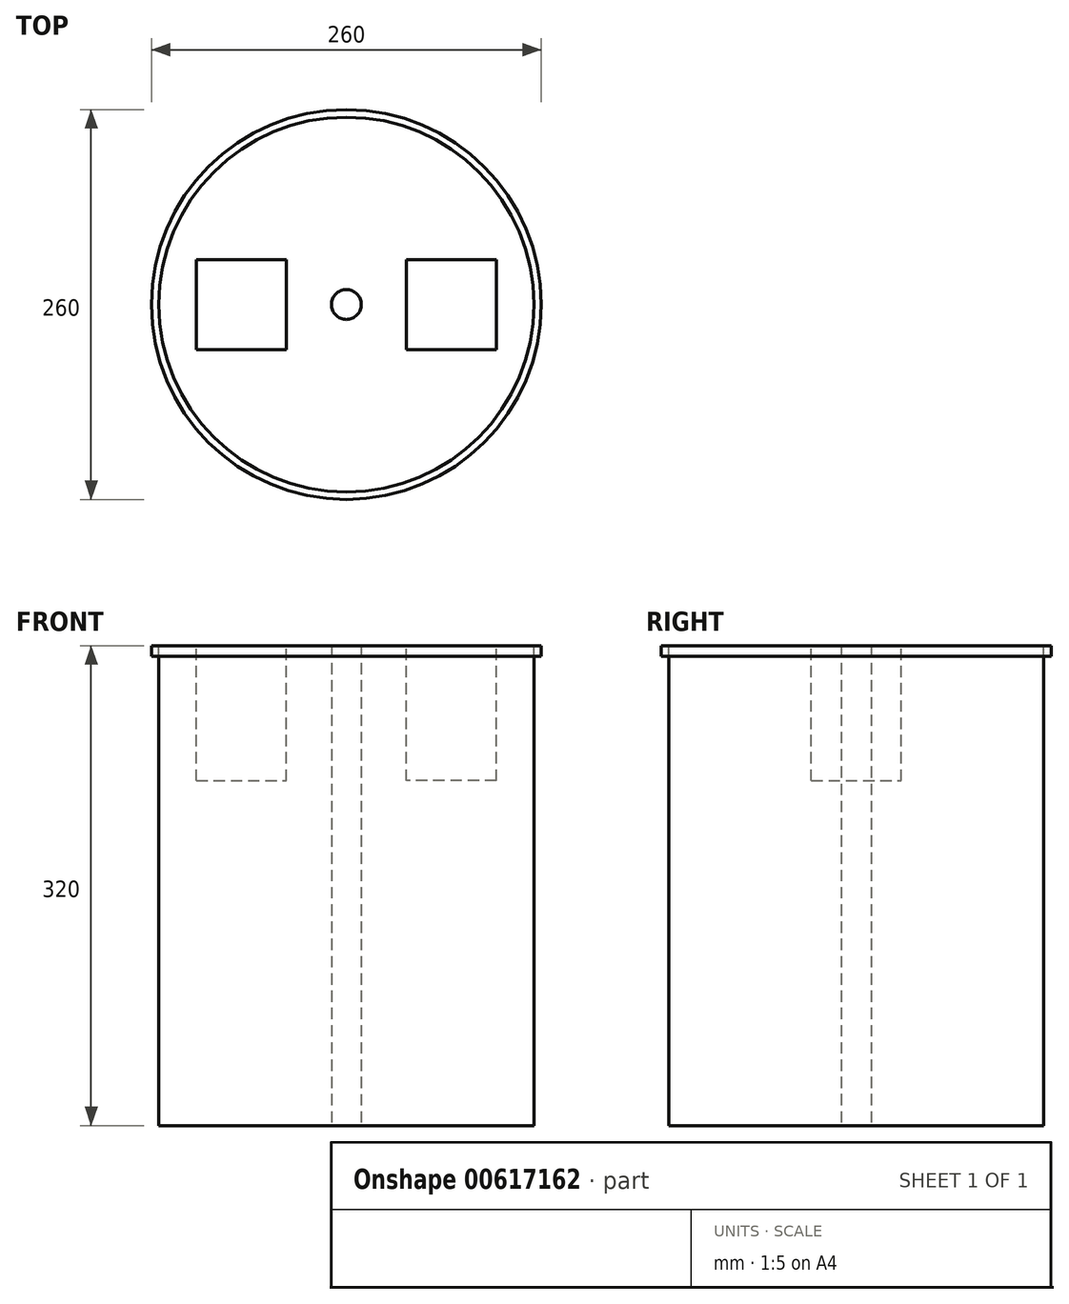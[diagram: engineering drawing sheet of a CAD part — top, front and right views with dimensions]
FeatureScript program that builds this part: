
annotation { "Feature Type Name" : "Feature", "Feature Type Description" : "" }
export const myFeature = defineFeature(function(context is Context, id is Id, definition is map)
    precondition{}
    {
        {
            var Q0;
            Q0=qCreatedBy(makeId("Top.planeOp"),FACE);
            var sketch = newSketch(context, id + "F0", { "sketchPlane" : qUnion([Q0])});
            skCircle(sketch, "E0", {"center": v(0, 0) * mm, "radius": 125 * mm});
            skCircle(sketch, "E1", {"center": v(0, 0) * mm, "radius": 9.95 * mm});
            skSolve(sketch);
        }
        {
            var Q0;
            Q0=makeQuery(id+"F0.imprint","IMPRINT",FACE,{"disambiguationData":[TD([[makeQuery(id+"F0.imprint","IMPRINT",EDGE,{"derivedFrom":sQuery(id+"F0.wireOp",EDGE,"E0")}),1.0]])]});
            extrude(context, id + "F1", {"entities" : qUnion([Q0]), "depth" : 320 * mm, "offsetDistance" : 25 * mm});
        }
        {
            var Q0;
            Q0=makeQuery(id+"F1.opExtrude","CAP_FACE",FACE,{"disambiguationData":[OSD([sQuery(id+"F0.wireOp",EDGE,"E0")])],"isStart":false});
            var sketch = newSketch(context, id + "F2", { "sketchPlane" : qUnion([Q0])});
            skCircle(sketch, "E2", {"center": v(0, 0) * mm, "radius": 130 * mm});
            skSolve(sketch);
        }
        {
            var Q0;
            Q0=makeQuery(id+"F2.imprint","IMPRINT",FACE,{"disambiguationData":[TD([[makeQuery(id+"F2.imprint","IMPRINT",EDGE,{"derivedFrom":sQuery(id+"F2.wireOp",EDGE,"E2")}),1.0]])]});
            extrude(context, id + "F3", {"entities" : qUnion([Q0]), "oppositeDirection" : true, "depth" : 7.1 * mm, "offsetDistance" : 25 * mm});
        }
        {
            var Q0;
            Q0=makeQuery(id+"F1.opExtrude","CAP_FACE",FACE,{"disambiguationData":[OSD([sQuery(id+"F0.wireOp",EDGE,"E0")])],"isStart":false});
            var sketch = newSketch(context, id + "F4", { "sketchPlane" : qUnion([Q0])});
            skCircle(sketch, "E3", {"center": v(0, 0) * mm, "radius": 0.92 * mm});
            skSolve(sketch);
        }
        {
            var Q0;
            Q0 = qSketchRegion(id + "F4", true);
            extrude(context, id + "F5", {"entities" : qUnion([Q0]), "operationType" : NewBodyOperationType.REMOVE, "oppositeDirection" : true, "depth" : 25 * mm, "offsetDistance" : 25 * mm});
        }
        {
            var Q0;
            Q0=makeQuery(id+"F1.opExtrude","CAP_FACE",FACE,{"disambiguationData":[OSD([sQuery(id+"F0.wireOp",EDGE,"E0"),sQuery(id+"F0.wireOp",EDGE,"E1")])],"isStart":false});
            var sketch = newSketch(context, id + "F6", { "sketchPlane" : qUnion([Q0])});
            skLineSegment(sketch, "E4.bottom", {"start": v(99.95, -30) * mm, "end": v(39.95, -30) * mm});
            skLineSegment(sketch, "E4.top", {"start": v(99.95, 30) * mm, "end": v(39.95, 30) * mm});
            skLineSegment(sketch, "E4.left", {"start": v(99.95, -30) * mm, "end": v(99.95, 30) * mm});
            skLineSegment(sketch, "E4.right", {"start": v(39.95, -30) * mm, "end": v(39.95, 30) * mm});
            skPoint(sketch, "E4.middle", {"position": v(69.95, 0) * mm});
            skLineSegment(sketch, "E5.bottom", {"start": v(-99.95, 30) * mm, "end": v(-39.95, 30) * mm});
            skLineSegment(sketch, "E5.top", {"start": v(-99.95, -30) * mm, "end": v(-39.95, -30) * mm});
            skLineSegment(sketch, "E5.left", {"start": v(-99.95, 30) * mm, "end": v(-99.95, -30) * mm});
            skLineSegment(sketch, "E5.right", {"start": v(-39.95, 30) * mm, "end": v(-39.95, -30) * mm});
            skPoint(sketch, "E5.middle", {"position": v(-69.95, 0) * mm});
            skSolve(sketch);
        }
        {
            var Q0;
            Q0=makeQuery(id+"F6.imprint","IMPRINT",FACE,{"disambiguationData":[TD([[makeQuery(id+"F6.imprint","IMPRINT",EDGE,{"derivedFrom":sQuery(id+"F6.wireOp",EDGE,"E5.bottom")}),-1.0]])]});
            var Q1;
            Q1=makeQuery(id+"F6.imprint","IMPRINT",FACE,{"disambiguationData":[TD([[makeQuery(id+"F6.imprint","IMPRINT",EDGE,{"derivedFrom":sQuery(id+"F6.wireOp",EDGE,"E4.bottom")}),-1.0]])]});
            extrude(context, id + "F7", {"entities" : qUnion([Q0, Q1]), "operationType" : NewBodyOperationType.REMOVE, "oppositeDirection" : true, "depth" : 90 * mm, "offsetDistance" : 25 * mm});
        }
    });
